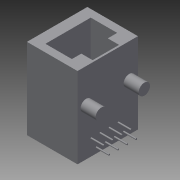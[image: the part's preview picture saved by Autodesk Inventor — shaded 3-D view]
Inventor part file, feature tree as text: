
AUTODESK INVENTOR PART (.ipt)
format: ipt  version: 2015 (Build 190159000, 159)  size: 142,848 bytes
history: native  units: in
note: dims shown in document units (in); Inventor stores cm internally (conversion verified against a paired STEP export)
features: extrude x4, sketch x4
ambient origin geometry x8: Origin, YZ Plane, XZ Plane, XY Plane, X Axis, Y Axis, Z Axis, Center Point
bodies: Solid1 (feature_tree)
feature tree (8):
  extrude  "Extrusion1"  Depth=0.6299in
  extrude  "Extrusion2"  Depth=0.4724in
  extrude  "Extrusion3"  Depth=0.2756in
  extrude  "Extrusion4"  Depth=0.2756in
  sketch  "Sketch1"  dims[d0=0.5276in d1=0.6299in]
  sketch  "Sketch2"  dims[d2=0.8425in d3=0.0in d4=0.4724in]
  sketch  "Sketch3"  dims[d5=0.2756in d6=0.2756in]
  sketch  "Sketch4"  dims[d7=0.1181in d8=0.2756in d9=0.0984in d10=0.0984in d11=0.0787in d12=0.0787in d13=0.1142in d14=0.4724in d15=0.0in d16=0.1181in d17=0.1181in d18=0.3543in d19=0.3543in d20=0.0906in d21=0.0906in d22=0.1575in d23=0.0in d24=0.0157in d25=0.0157in d26=0.1417in d27=0.0945in d28=0.0157in d29=0.0157in d30=0.0945in d31=0.0945in d32=0.0in d33=0.0in d34=0.0in d35=0.1654in d36=0.0551in d37=0.0157in d38=0.0157in d39=0.0157in d40=0.0157in d41=0.0551in d42=0.0945in d43=0.0945in d44=0.0945in d45=0.1339in d46=0.0in]
